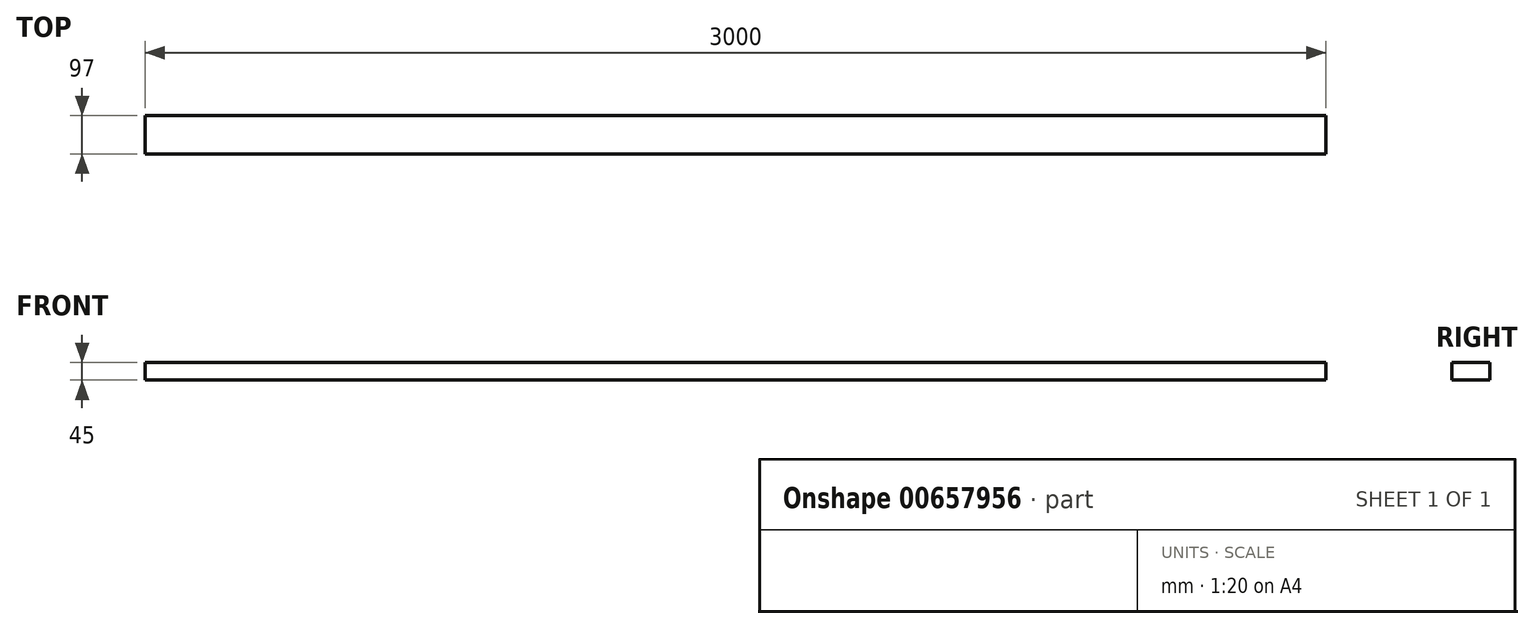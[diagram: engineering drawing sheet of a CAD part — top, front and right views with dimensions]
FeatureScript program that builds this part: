
annotation { "Feature Type Name" : "Feature", "Feature Type Description" : "" }
export const myFeature = defineFeature(function(context is Context, id is Id, definition is map)
    precondition{}
    {
        {
            var Q0;
            Q0=qCreatedBy(makeId("Right.planeOp"),FACE);
            var sketch = newSketch(context, id + "F0", { "sketchPlane" : qUnion([Q0])});
            skLineSegment(sketch, "E0.bottom", {"start": v(-48.5, -22.5) * mm, "end": v(48.5, -22.5) * mm});
            skLineSegment(sketch, "E0.top", {"start": v(-48.5, 22.5) * mm, "end": v(48.5, 22.5) * mm});
            skLineSegment(sketch, "E0.left", {"start": v(-48.5, -22.5) * mm, "end": v(-48.5, 22.5) * mm});
            skLineSegment(sketch, "E0.right", {"start": v(48.5, -22.5) * mm, "end": v(48.5, 22.5) * mm});
            skPoint(sketch, "E0.middle", {"position": v(0, 0) * mm});
            skSolve(sketch);
        }
        {
            var Q0;
            Q0 = qSketchRegion(id + "F0", true);
            extrude(context, id + "F1", {"entities" : qUnion([Q0]), "endBound" : BoundingType.SYMMETRIC, "depth" : 3000 * mm, "offsetDistance" : 25 * mm});
        }
    });
